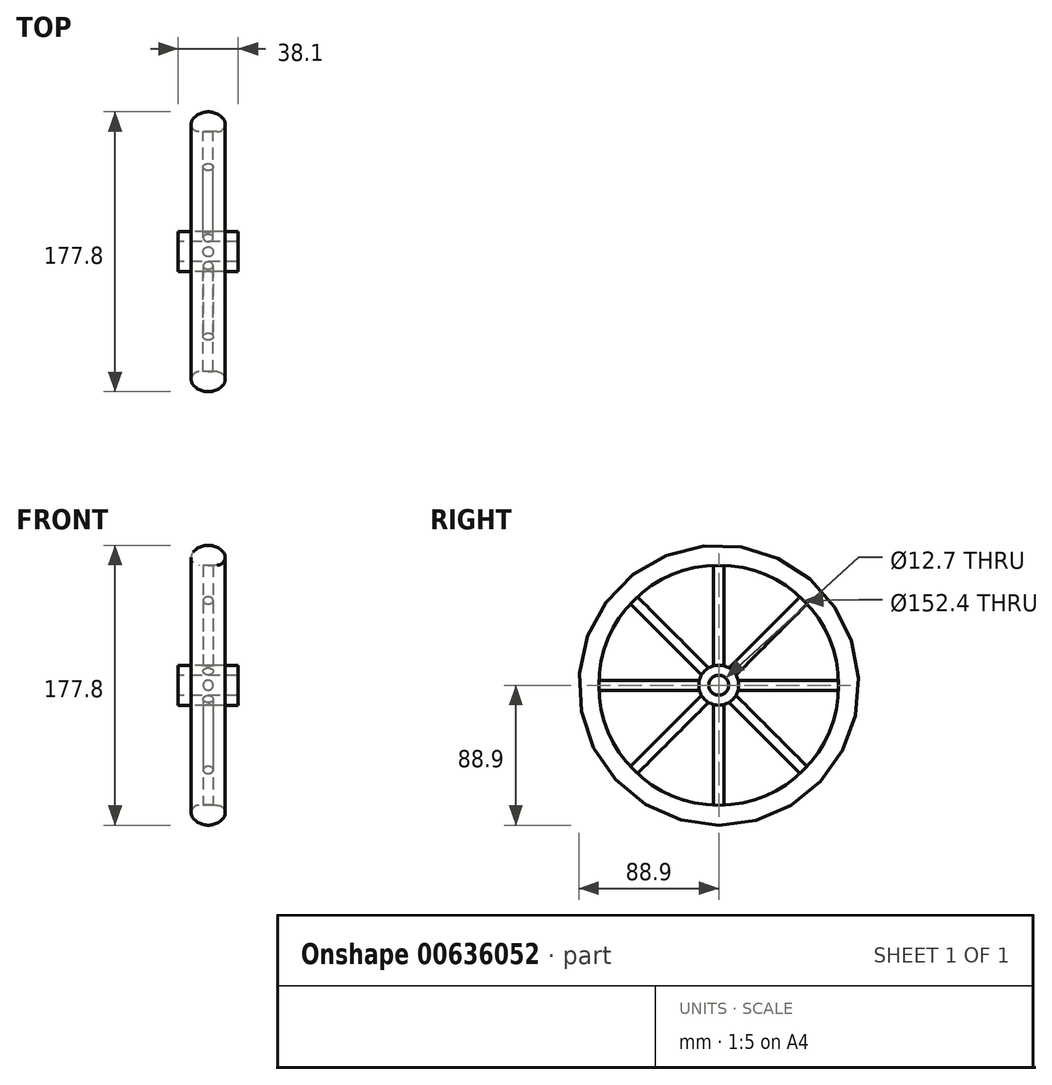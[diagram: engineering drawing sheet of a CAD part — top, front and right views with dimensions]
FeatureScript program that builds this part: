
annotation { "Feature Type Name" : "Feature", "Feature Type Description" : "" }
export const myFeature = defineFeature(function(context is Context, id is Id, definition is map)
    precondition{}
    {
        {
            var Q0;
            Q0=qCreatedBy(makeId("Right.planeOp"),FACE);
            var sketch = newSketch(context, id + "F0", { "sketchPlane" : qUnion([Q0])});
            skCircle(sketch, "E0", {"center": v(0, 0) * mm, "radius": 88.9 * mm});
            skCircle(sketch, "E1", {"center": v(0, 0) * mm, "radius": 76.2 * mm});
            skCircle(sketch, "E2", {"center": v(0, 0) * mm, "radius": 6.35 * mm});
            skCircle(sketch, "E3", {"center": v(0, 0) * mm, "radius": 12.7 * mm});
            skLineSegment(sketch, "E4.0", {"start": v(-3.18, 12.3) * mm, "end": v(-3.18, 76.13) * mm});
            skLineSegment(sketch, "E5.0", {"start": v(3.17, 12.3) * mm, "end": v(3.17, 76.13) * mm});
            skLineSegment(sketch, "E6.1.0", {"start": v(-6.45, 10.94) * mm, "end": v(-51.59, 56.08) * mm});
            skLineSegment(sketch, "E6.1.1", {"start": v(-10.94, 6.45) * mm, "end": v(-56.08, 51.59) * mm});
            skLineSegment(sketch, "E6.2.0", {"start": v(-12.3, 3.17) * mm, "end": v(-76.13, 3.18) * mm});
            skLineSegment(sketch, "E6.2.1", {"start": v(-12.3, -3.18) * mm, "end": v(-76.13, -3.17) * mm});
            skLineSegment(sketch, "E6.3.0", {"start": v(-10.94, -6.45) * mm, "end": v(-56.08, -51.59) * mm});
            skLineSegment(sketch, "E6.3.1", {"start": v(-6.45, -10.94) * mm, "end": v(-51.59, -56.08) * mm});
            skLineSegment(sketch, "E6.4.0", {"start": v(-3.17, -12.3) * mm, "end": v(-3.18, -76.13) * mm});
            skLineSegment(sketch, "E6.4.1", {"start": v(3.18, -12.3) * mm, "end": v(3.17, -76.13) * mm});
            skLineSegment(sketch, "E6.5.0", {"start": v(6.45, -10.94) * mm, "end": v(51.59, -56.08) * mm});
            skLineSegment(sketch, "E6.5.1", {"start": v(10.94, -6.45) * mm, "end": v(56.08, -51.59) * mm});
            skLineSegment(sketch, "E6.6.0", {"start": v(12.3, -3.17) * mm, "end": v(76.13, -3.18) * mm});
            skLineSegment(sketch, "E6.6.1", {"start": v(12.3, 3.18) * mm, "end": v(76.13, 3.17) * mm});
            skLineSegment(sketch, "E6.7.0", {"start": v(10.94, 6.45) * mm, "end": v(56.08, 51.59) * mm});
            skLineSegment(sketch, "E6.7.1", {"start": v(6.45, 10.94) * mm, "end": v(51.59, 56.08) * mm});
            skSolve(sketch);
        }
        {
            var Q0;
            Q0=makeQuery(id+"F0.imprint","IMPRINT",FACE,{"disambiguationData":[TD([[makeQuery(id+"F0.imprint","IMPRINT",EDGE,{"derivedFrom":sQuery(id+"F0.wireOp",EDGE,"E0")}),1.0]])]});
            extrude(context, id + "F1", {"entities" : qUnion([Q0]), "endBound" : BoundingType.SYMMETRIC, "depth" : 25.4 * mm, "offsetDistance" : 25.4 * mm});
        }
        {
            var Q0;
            Q0=makeQuery(id+"F0.imprint","IMPRINT",FACE,{"disambiguationData":[TD([[makeQuery(id+"F0.imprint","IMPRINT",EDGE,{"derivedFrom":sQuery(id+"F0.wireOp",EDGE,"E2")}),-1.0]])]});
            extrude(context, id + "F2", {"entities" : qUnion([Q0]), "endBound" : BoundingType.SYMMETRIC, "depth" : 38.1 * mm, "offsetDistance" : 25.4 * mm});
        }
        {
            var Q0;
            {var subQ0=sQuery(id+"F0.wireOp",EDGE,"E6.1.0");Q0=makeQuery(id+"F0.imprint","IMPRINT",FACE,{"disambiguationData":[TD([[makeQuery(id+"F0.imprint","IMPRINT",EDGE,{"derivedFrom":subQ0}),1.0]])]});}
            var Q1;
            {var subQ0=sQuery(id+"F0.wireOp",EDGE,"E4.0");Q1=makeQuery(id+"F0.imprint","IMPRINT",FACE,{"disambiguationData":[TD([[makeQuery(id+"F0.imprint","IMPRINT",EDGE,{"derivedFrom":subQ0}),-1.0]])]});}
            var Q2;
            {var subQ0=sQuery(id+"F0.wireOp",EDGE,"E6.7.0");Q2=makeQuery(id+"F0.imprint","IMPRINT",FACE,{"disambiguationData":[TD([[makeQuery(id+"F0.imprint","IMPRINT",EDGE,{"derivedFrom":subQ0}),1.0]])]});}
            var Q3;
            {var subQ0=sQuery(id+"F0.wireOp",EDGE,"E6.6.0");Q3=makeQuery(id+"F0.imprint","IMPRINT",FACE,{"disambiguationData":[TD([[makeQuery(id+"F0.imprint","IMPRINT",EDGE,{"derivedFrom":subQ0}),1.0]])]});}
            var Q4;
            {var subQ0=sQuery(id+"F0.wireOp",EDGE,"E6.2.0");Q4=makeQuery(id+"F0.imprint","IMPRINT",FACE,{"disambiguationData":[TD([[makeQuery(id+"F0.imprint","IMPRINT",EDGE,{"derivedFrom":subQ0}),1.0]])]});}
            var Q5;
            {var subQ0=sQuery(id+"F0.wireOp",EDGE,"E6.3.0");Q5=makeQuery(id+"F0.imprint","IMPRINT",FACE,{"disambiguationData":[TD([[makeQuery(id+"F0.imprint","IMPRINT",EDGE,{"derivedFrom":subQ0}),1.0]])]});}
            var Q6;
            {var subQ0=sQuery(id+"F0.wireOp",EDGE,"E6.5.0");Q6=makeQuery(id+"F0.imprint","IMPRINT",FACE,{"disambiguationData":[TD([[makeQuery(id+"F0.imprint","IMPRINT",EDGE,{"derivedFrom":subQ0}),1.0]])]});}
            var Q7;
            {var subQ0=sQuery(id+"F0.wireOp",EDGE,"E6.4.0");Q7=makeQuery(id+"F0.imprint","IMPRINT",FACE,{"disambiguationData":[TD([[makeQuery(id+"F0.imprint","IMPRINT",EDGE,{"derivedFrom":subQ0}),1.0]])]});}
            extrude(context, id + "F3", {"entities" : qUnion([Q0, Q1, Q2, Q3, Q4, Q5, Q6, Q7]), "endBound" : BoundingType.SYMMETRIC, "depth" : 6.35 * mm, "offsetDistance" : 25.4 * mm});
        }
        {
            var Q0;
            Q0=makeQuery(id+"F3.opExtrude","CAP_EDGE",EDGE,{"disambiguationData":[OSD([sQuery(id+"F0.wireOp",EDGE,"E6.1.0")])],"isStart":false});
            var Q1;
            Q1=makeQuery(id+"F3.opExtrude","CAP_EDGE",EDGE,{"disambiguationData":[OSD([sQuery(id+"F0.wireOp",EDGE,"E6.1.0")])],"isStart":true});
            var Q2;
            Q2=makeQuery(id+"F3.opExtrude","CAP_EDGE",EDGE,{"disambiguationData":[OSD([sQuery(id+"F0.wireOp",EDGE,"E4.0")])],"isStart":false});
            var Q3;
            Q3=makeQuery(id+"F3.opExtrude","CAP_EDGE",EDGE,{"disambiguationData":[OSD([sQuery(id+"F0.wireOp",EDGE,"E5.0")])],"isStart":false});
            var Q4;
            Q4=makeQuery(id+"F3.opExtrude","CAP_EDGE",EDGE,{"disambiguationData":[OSD([sQuery(id+"F0.wireOp",EDGE,"E5.0")])],"isStart":true});
            var Q5;
            Q5=makeQuery(id+"F3.opExtrude","CAP_EDGE",EDGE,{"disambiguationData":[OSD([sQuery(id+"F0.wireOp",EDGE,"E6.7.1")])],"isStart":false});
            var Q6;
            Q6=makeQuery(id+"F3.opExtrude","CAP_EDGE",EDGE,{"disambiguationData":[OSD([sQuery(id+"F0.wireOp",EDGE,"E6.7.0")])],"isStart":false});
            var Q7;
            Q7=makeQuery(id+"F3.opExtrude","CAP_EDGE",EDGE,{"disambiguationData":[OSD([sQuery(id+"F0.wireOp",EDGE,"E6.6.1")])],"isStart":true});
            var Q8;
            Q8=makeQuery(id+"F3.opExtrude","CAP_EDGE",EDGE,{"disambiguationData":[OSD([sQuery(id+"F0.wireOp",EDGE,"E6.6.1")])],"isStart":false});
            var Q9;
            Q9=makeQuery(id+"F3.opExtrude","CAP_EDGE",EDGE,{"disambiguationData":[OSD([sQuery(id+"F0.wireOp",EDGE,"E6.6.0")])],"isStart":false});
            var Q10;
            Q10=makeQuery(id+"F3.opExtrude","CAP_EDGE",EDGE,{"disambiguationData":[OSD([sQuery(id+"F0.wireOp",EDGE,"E6.2.0")])],"isStart":true});
            var Q11;
            Q11=makeQuery(id+"F3.opExtrude","CAP_EDGE",EDGE,{"disambiguationData":[OSD([sQuery(id+"F0.wireOp",EDGE,"E6.2.0")])],"isStart":false});
            var Q12;
            Q12=makeQuery(id+"F3.opExtrude","CAP_EDGE",EDGE,{"disambiguationData":[OSD([sQuery(id+"F0.wireOp",EDGE,"E6.2.1")])],"isStart":false});
            var Q13;
            Q13=makeQuery(id+"F3.opExtrude","CAP_EDGE",EDGE,{"disambiguationData":[OSD([sQuery(id+"F0.wireOp",EDGE,"E6.3.0")])],"isStart":false});
            var Q14;
            Q14=makeQuery(id+"F3.opExtrude","CAP_EDGE",EDGE,{"disambiguationData":[OSD([sQuery(id+"F0.wireOp",EDGE,"E6.3.1")])],"isStart":false});
            var Q15;
            Q15=makeQuery(id+"F3.opExtrude","CAP_EDGE",EDGE,{"disambiguationData":[OSD([sQuery(id+"F0.wireOp",EDGE,"E6.3.1")])],"isStart":true});
            var Q16;
            Q16=makeQuery(id+"F3.opExtrude","CAP_EDGE",EDGE,{"disambiguationData":[OSD([sQuery(id+"F0.wireOp",EDGE,"E6.4.0")])],"isStart":false});
            var Q17;
            Q17=makeQuery(id+"F3.opExtrude","CAP_EDGE",EDGE,{"disambiguationData":[OSD([sQuery(id+"F0.wireOp",EDGE,"E6.4.1")])],"isStart":false});
            var Q18;
            Q18=makeQuery(id+"F3.opExtrude","CAP_EDGE",EDGE,{"disambiguationData":[OSD([sQuery(id+"F0.wireOp",EDGE,"E6.4.1")])],"isStart":true});
            var Q19;
            Q19=makeQuery(id+"F3.opExtrude","CAP_EDGE",EDGE,{"disambiguationData":[OSD([sQuery(id+"F0.wireOp",EDGE,"E6.5.0")])],"isStart":false});
            var Q20;
            Q20=makeQuery(id+"F3.opExtrude","CAP_EDGE",EDGE,{"disambiguationData":[OSD([sQuery(id+"F0.wireOp",EDGE,"E6.5.1")])],"isStart":false});
            var Q21;
            Q21=makeQuery(id+"F3.opExtrude","CAP_EDGE",EDGE,{"disambiguationData":[OSD([sQuery(id+"F0.wireOp",EDGE,"E6.5.1")])],"isStart":true});
            var Q22;
            Q22=makeQuery(id+"F3.opExtrude","CAP_EDGE",EDGE,{"disambiguationData":[OSD([sQuery(id+"F0.wireOp",EDGE,"E6.7.0")])],"isStart":true});
            var Q23;
            Q23=makeQuery(id+"F3.opExtrude","CAP_EDGE",EDGE,{"disambiguationData":[OSD([sQuery(id+"F0.wireOp",EDGE,"E6.7.1")])],"isStart":true});
            var Q24;
            Q24=makeQuery(id+"F3.opExtrude","CAP_EDGE",EDGE,{"disambiguationData":[OSD([sQuery(id+"F0.wireOp",EDGE,"E6.6.0")])],"isStart":true});
            var Q25;
            Q25=makeQuery(id+"F3.opExtrude","CAP_EDGE",EDGE,{"disambiguationData":[OSD([sQuery(id+"F0.wireOp",EDGE,"E6.5.0")])],"isStart":true});
            var Q26;
            Q26=makeQuery(id+"F3.opExtrude","CAP_EDGE",EDGE,{"disambiguationData":[OSD([sQuery(id+"F0.wireOp",EDGE,"E4.0")])],"isStart":true});
            var Q27;
            Q27=makeQuery(id+"F3.opExtrude","CAP_EDGE",EDGE,{"disambiguationData":[OSD([sQuery(id+"F0.wireOp",EDGE,"E6.4.0")])],"isStart":true});
            var Q28;
            Q28=makeQuery(id+"F3.opExtrude","CAP_EDGE",EDGE,{"disambiguationData":[OSD([sQuery(id+"F0.wireOp",EDGE,"E6.3.0")])],"isStart":true});
            var Q29;
            Q29=makeQuery(id+"F3.opExtrude","CAP_EDGE",EDGE,{"disambiguationData":[OSD([sQuery(id+"F0.wireOp",EDGE,"E6.2.1")])],"isStart":true});
            var Q30;
            Q30=makeQuery(id+"F3.opExtrude","CAP_EDGE",EDGE,{"disambiguationData":[OSD([sQuery(id+"F0.wireOp",EDGE,"E6.1.1")])],"isStart":false});
            var Q31;
            Q31=makeQuery(id+"F3.opExtrude","CAP_EDGE",EDGE,{"disambiguationData":[OSD([sQuery(id+"F0.wireOp",EDGE,"E6.1.1")])],"isStart":true});
            fillet(context, id + "F4", {"entities" : qUnion([Q0, Q1, Q2, Q3, Q4, Q5, Q6, Q7, Q8, Q9, Q10, Q11, Q12, Q13, Q14, Q15, Q16, Q17, Q18, Q19, Q20, Q21, Q22, Q23, Q24, Q25, Q26, Q27, Q28, Q29, Q30, Q31]), "radius" : 3.17 * mm, "tangentPropagation" : true, "allowEdgeOverflow" : false});
        }
        {
            var Q0;
            Q0=makeQuery(id+"F1.opExtrude","CAP_EDGE",EDGE,{"disambiguationData":[OSD([sQuery(id+"F0.wireOp",EDGE,"E0")])],"isStart":false});
            var Q1;
            Q1=makeQuery(id+"F1.opExtrude","CAP_EDGE",EDGE,{"disambiguationData":[OSD([sQuery(id+"F0.wireOp",EDGE,"E0")])],"isStart":true});
            fillet(context, id + "F5", {"entities" : qUnion([Q0, Q1]), "radius" : 12.7 * mm, "tangentPropagation" : true, "allowEdgeOverflow" : false});
        }
        {
            var Q0;
            Q0=makeQuery(id+"F5.opFillet","BLEND_EDGE",EDGE,{"blendedFrom":[makeQuery(id+"F1.opExtrude","CAP_EDGE",EDGE,{"disambiguationData":[OSD([sQuery(id+"F0.wireOp",EDGE,"E0")])],"isStart":true}),makeQuery(id+"F1.opExtrude","SWEPT_FACE",FACE,{"disambiguationData":[OSD([sQuery(id+"F0.wireOp",EDGE,"E1")])]})],"blendedInto":[makeQuery(id+"F1.opExtrude","SWEPT_FACE",FACE,{"disambiguationData":[OSD([sQuery(id+"F0.wireOp",EDGE,"E1")])]})]});
            var Q1;
            Q1=makeQuery(id+"F5.opFillet","BLEND_EDGE",EDGE,{"blendedFrom":[makeQuery(id+"F1.opExtrude","CAP_EDGE",EDGE,{"disambiguationData":[OSD([sQuery(id+"F0.wireOp",EDGE,"E0")])],"isStart":false}),makeQuery(id+"F1.opExtrude","SWEPT_FACE",FACE,{"disambiguationData":[OSD([sQuery(id+"F0.wireOp",EDGE,"E1")])]})],"blendedInto":[makeQuery(id+"F1.opExtrude","SWEPT_FACE",FACE,{"disambiguationData":[OSD([sQuery(id+"F0.wireOp",EDGE,"E1")])]})]});
            fillet(context, id + "F6", {"entities" : qUnion([Q0, Q1]), "radius" : 5.08 * mm, "tangentPropagation" : true, "allowEdgeOverflow" : false});
        }
    });
